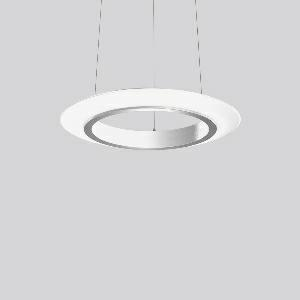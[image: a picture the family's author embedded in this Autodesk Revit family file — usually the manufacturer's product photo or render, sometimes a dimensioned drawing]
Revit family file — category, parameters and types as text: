
# Revit family: ring_of_fire_p_311669_004_76_4ef7
name_source: partatom
category: Lighting Fixtures
units: mm (PartAtom-declared; Revit-internal decimal feet)

## family parameters
Cut with Voids When Loaded = No
Host = Face
Light Source = No
Part Type = Normal
Room Calculation Point = No
Round Connector Dimension = Use Diameter
Shared = No

## types (1)
- RING OF FIRE P (1 x LED Modul 830, 2800 lm, 3000)
    Apparent Load = 28 VA
    CIE Flux Codes = 43 72 89 54 100
    Color Rendering = 80
    Color Temperature = 3000
    Default Elevation = 1800 mm
    Description = Series: RING OF FIRE
A uniquely shaped pendant luminaire with elliptical glass. Supporting ring made of anodised aluminium. Canopy aluminium anodised. Opal glass: mouth-blown, satin finish. Suitable for pendant. 3-point steel cable suspension, steplessly adjustable. Special lengths available on request. For pendant lengths of up to 2 m, power is supplied through a suspension cable. For pendant lengths of 2 m and more, power must be supplied through a separate cable. Converter integrated in the canopy. TouchDim sensor capable. Light and/or presence sensors can be integrated. 
Colour: anodised aluminium
Diameter: 495 mm
Height: 55 mm
Suspension length: 500-1200 mm
Lamp: LED
Socket: without socket
Colour temperature: 3000K
Colour rendering index (CRI): 80
System power: 28 W
Rated luminous flux: 2800 lm
Luminous efficiency: 100 lm/W
Control gear: Converter, dimmable, DALI
Protection class: I
Type of protection: IP 20
    Height = 55 mm
    Lamp = 1 x LED Modul 830
    Lamp Light Flux = 2800 lm
    Lamp count = 1
    Length = 495 mm
    Lifetime = 50000 h
    Luminous efficacy = 100 lm/W
    Manufacturer = RZB
    ModVariant = No
    Model = 311669.004.76
    Mounting Place = Ceiling
    Mounting Type = Pendant
    Number of Poles = 1
    OnlyDefault = Yes
    Power Factor = 1
    Product Name = RING OF FIRE P
    Product group = Pendant luminaires
    ProductGroupID = 902
    Protection Class = Protection class I
    Protection Degree = IP 20
    RLX_Detail_Level = 1
    RLX_Emergency_Light_Flux = 0 lm
    RLX_Emergency_Type = 0
    RLX_Emergency_Type_DB = No
    RlxData = <blob elided: 38017 chars, md5=08e706af>
    Socket = socket
    Standby Power = 0 W
    System Light Flux = 2800 lm
    System Power = 28 W
    Type Comments = Product without accessories
    Type Image = 311669.004.jpg
    URL = http://relux.com
    VarID = ---
    Voltage = 230 V
    Voltage Range = 220-240 V
    Weight = 0.00 kg
    Width = 0 mm  [stored 0 ft]

note: [stored X ft] marks values corroborated as IEEE doubles in the binary element streams (Revit-internal decimal feet)

## geometry (parser evidence)
native form markers: Blend x4, Sweep x11
no freeform markers — native parametric forms only
